# Revit family: Skylight_Architectural_ArtisticSkylight_RidgeGlass
name_source: partatom
category: Windows
units: mm (PartAtom-declared; Revit-internal decimal feet)

## family parameters
Classification Number = 23.30.30.17.21
Cut with Voids When Loaded = No
Host = Face
Room Calculation Point = No
Shared = No

## types (1)
- as Specified
    Air Infiltration = 0.06 cfm
    Assembly Code = B3020110
    Construction Details = http://arcat.com
    Curb Thickness = 0' - 1 1/2"
    Default Elevation = 0' - 0"
    Description = Artistic Skylights Fixed Continuous Skylight - Architectural Ridge Glass Model G-CU-P-CF-FF-VE x Unlimited
    Expected Lifespan (Years) = 0
    Green Building-LEED = http://arcat.com
    Height = 4' - 0"
    Keynote = 8600
    Maintenance Schedule (Months) = 0
    Manufacturer = Artistic Skylight Domes Ltd.
    Manufacturer Fax = 416-747-6630
    Manufacturer Website = http://artisticskylight.com
    Model = G-CU-P-CF-FF-VE x Unlimited
    Product Data = http://arcat.com
    Revision = R1_02_2014
    Rough Height = 3' - 9"
    Sales Information = http://artisticskylight.com
    Send Message = http://arcat.com
    Specification = http://arcat.com
    Standards Conformance = Class A Type 2 or Type 3
    Structural Test Pressure = Glazing +/- 60 psf
    Test Data = http://artisticskylight.com
    URL = http://artisticskylight.com
    Warranty Duration (Years) = 0
    Water Penetration = No Penetration at 12 psf

## geometry (parser evidence)
native form markers: Blend x12, Sweep x9
no freeform markers — native parametric forms only
